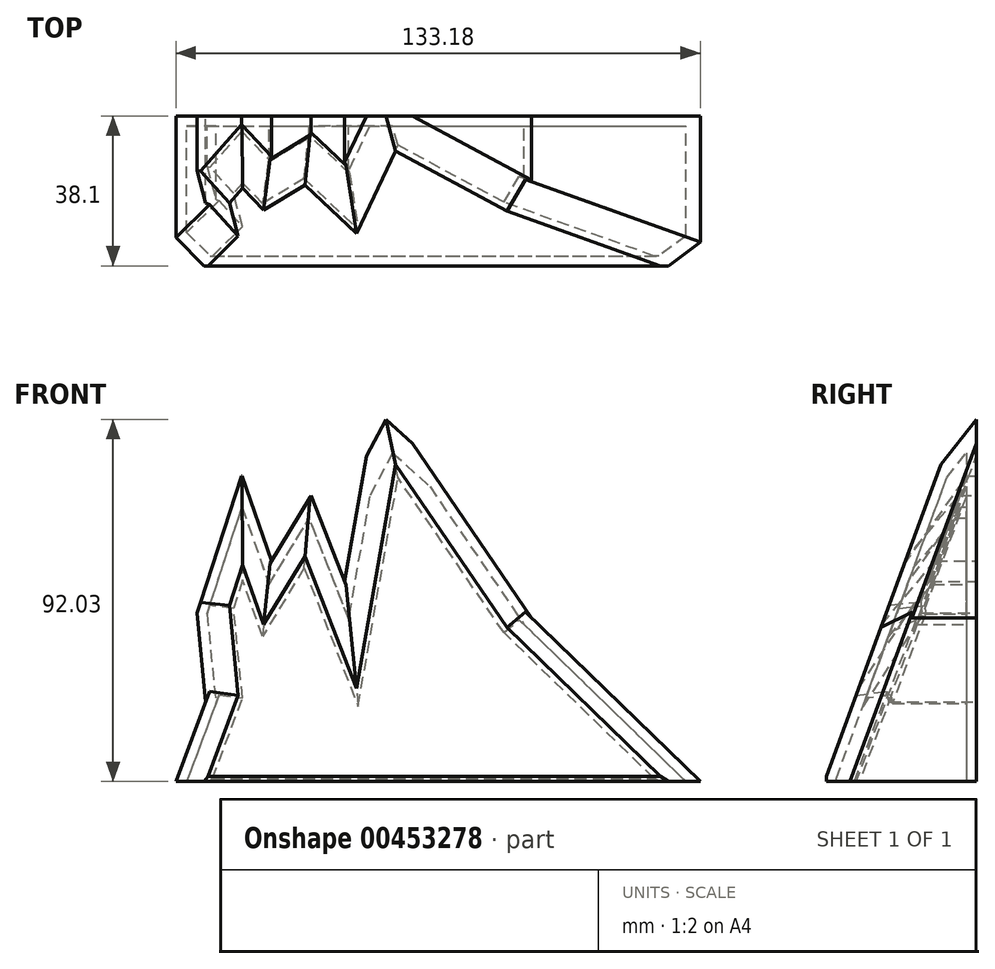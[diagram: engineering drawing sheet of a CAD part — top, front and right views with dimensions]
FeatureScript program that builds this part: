
annotation { "Feature Type Name" : "Feature", "Feature Type Description" : "" }
export const myFeature = defineFeature(function(context is Context, id is Id, definition is map)
    precondition{}
    {
        {
            var Q0;
            Q0=qCreatedBy(makeId("Front.planeOp"),FACE);
            var sketch = newSketch(context, id + "F0", { "sketchPlane" : qUnion([Q0])});
            skLineSegment(sketch, "E0", {"start": v(-64.04, -23.03) * mm, "end": v(69.14, -23.03) * mm});
            skLineSegment(sketch, "E1", {"start": v(-12.84, 75.84) * mm, "end": v(-21.19, 27.85) * mm});
            skLineSegment(sketch, "E2", {"start": v(-21.19, 27.85) * mm, "end": v(-29.7, 49.6) * mm});
            skLineSegment(sketch, "E3", {"start": v(-58.74, 19.82) * mm, "end": v(-56.5, -2.8) * mm});
            skLineSegment(sketch, "E4", {"start": v(-56.5, -2.8) * mm, "end": v(-64.04, -23.03) * mm});
            skLineSegment(sketch, "E5", {"start": v(-58.74, 19.82) * mm, "end": v(-47.35, 54.65) * mm});
            skLineSegment(sketch, "E6", {"start": v(-47.35, 54.65) * mm, "end": v(-39.8, 32.98) * mm});
            skLineSegment(sketch, "E7", {"start": v(-39.8, 32.98) * mm, "end": v(-29.7, 49.6) * mm});
            skLineSegment(sketch, "E8", {"start": v(-12.84, 75.84) * mm, "end": v(26.32, 18.54) * mm});
            skLineSegment(sketch, "E9", {"start": v(26.32, 18.54) * mm, "end": v(69.14, -23.03) * mm});
            skSolve(sketch);
        }
        {
            var Q0;
            Q0 = qSketchRegion(id + "F0", true);
            extrude(context, id + "F1", {"entities" : qUnion([Q0]), "depth" : 38.1 * mm});
        }
        {
            var Q0;
            Q0=qCreatedBy(makeId("Right.planeOp"),FACE);
            cPlane(context, id + "F2", {"entities" : qUnion([Q0]), "cplaneType" : CPlaneType.OFFSET, "offset" : 76.2 * mm, "width" : 152.4 * mm, "height" : 152.4 * mm});
        }
        {
            var Q0;
            Q0=qCreatedBy(id+"F2.planeOp",FACE);
            var sketch = newSketch(context, id + "F3", { "sketchPlane" : qUnion([Q0])});
            skLineSegment(sketch, "E10", {"start": v(-38.62, -23.16) * mm, "end": v(-1.41, 77.93) * mm});
            skLineSegment(sketch, "E11", {"start": v(-1.41, 77.93) * mm, "end": v(-41.3, 77.93) * mm});
            skLineSegment(sketch, "E12", {"start": v(-41.3, 77.93) * mm, "end": v(-38.62, -23.16) * mm});
            skSolve(sketch);
        }
        {
            var Q0;
            Q0 = qSketchRegion(id + "F3", true);
            extrude(context, id + "F4", {"entities" : qUnion([Q0]), "operationType" : NewBodyOperationType.REMOVE, "endBound" : BoundingType.THROUGH_ALL, "oppositeDirection" : true, "depth" : 25.4 * mm});
        }
        {
            var Q0;
            Q0=makeQuery(id+"F4.boolean.opBoolean","INTERSECT",EDGE,{"derivedFrom":[makeQuery(id+"F1.opExtrude","SWEPT_FACE",FACE,{"disambiguationData":[OSD([sQuery(id+"F0.wireOp",EDGE,"E5")])]}),makeQuery(id+"F4.opExtrude","SWEPT_FACE",FACE,{"disambiguationData":[OSD([sQuery(id+"F3.wireOp",EDGE,"E10")])]})]});
            var Q1;
            Q1=makeQuery(id+"F4.boolean.opBoolean","INTERSECT",EDGE,{"derivedFrom":[makeQuery(id+"F1.opExtrude","SWEPT_FACE",FACE,{"disambiguationData":[OSD([sQuery(id+"F0.wireOp",EDGE,"E6")])]}),makeQuery(id+"F4.opExtrude","SWEPT_FACE",FACE,{"disambiguationData":[OSD([sQuery(id+"F3.wireOp",EDGE,"E10")])]})]});
            var Q2;
            Q2=makeQuery(id+"F4.boolean.opBoolean","INTERSECT",EDGE,{"derivedFrom":[makeQuery(id+"F1.opExtrude","SWEPT_FACE",FACE,{"disambiguationData":[OSD([sQuery(id+"F0.wireOp",EDGE,"E7")])]}),makeQuery(id+"F4.opExtrude","SWEPT_FACE",FACE,{"disambiguationData":[OSD([sQuery(id+"F3.wireOp",EDGE,"E10")])]})]});
            var Q3;
            Q3=makeQuery(id+"F4.boolean.opBoolean","INTERSECT",EDGE,{"derivedFrom":[makeQuery(id+"F1.opExtrude","SWEPT_FACE",FACE,{"disambiguationData":[OSD([sQuery(id+"F0.wireOp",EDGE,"E2")])]}),makeQuery(id+"F4.opExtrude","SWEPT_FACE",FACE,{"disambiguationData":[OSD([sQuery(id+"F3.wireOp",EDGE,"E10")])]})]});
            var Q4;
            Q4=makeQuery(id+"F4.boolean.opBoolean","INTERSECT",EDGE,{"derivedFrom":[makeQuery(id+"F1.opExtrude","SWEPT_FACE",FACE,{"disambiguationData":[OSD([sQuery(id+"F0.wireOp",EDGE,"E1")])]}),makeQuery(id+"F4.opExtrude","SWEPT_FACE",FACE,{"disambiguationData":[OSD([sQuery(id+"F3.wireOp",EDGE,"E10")])]})]});
            var Q5;
            Q5=makeQuery(id+"F4.boolean.opBoolean","INTERSECT",EDGE,{"derivedFrom":[makeQuery(id+"F1.opExtrude","SWEPT_FACE",FACE,{"disambiguationData":[OSD([sQuery(id+"F0.wireOp",EDGE,"E8")])]}),makeQuery(id+"F4.opExtrude","SWEPT_FACE",FACE,{"disambiguationData":[OSD([sQuery(id+"F3.wireOp",EDGE,"E10")])]})]});
            var Q6;
            Q6=makeQuery(id+"F4.boolean.opBoolean","INTERSECT",EDGE,{"derivedFrom":[makeQuery(id+"F1.opExtrude","SWEPT_FACE",FACE,{"disambiguationData":[OSD([sQuery(id+"F0.wireOp",EDGE,"E9")])]}),makeQuery(id+"F4.opExtrude","SWEPT_FACE",FACE,{"disambiguationData":[OSD([sQuery(id+"F3.wireOp",EDGE,"E10")])]})]});
            var Q7;
            Q7=makeQuery(id+"F4.boolean.opBoolean","INTERSECT",EDGE,{"derivedFrom":[makeQuery(id+"F1.opExtrude","SWEPT_FACE",FACE,{"disambiguationData":[OSD([sQuery(id+"F0.wireOp",EDGE,"E4")])]}),makeQuery(id+"F4.opExtrude","SWEPT_FACE",FACE,{"disambiguationData":[OSD([sQuery(id+"F3.wireOp",EDGE,"E10")])]})]});
            var Q8;
            Q8=makeQuery(id+"F4.boolean.opBoolean","INTERSECT",EDGE,{"derivedFrom":[makeQuery(id+"F1.opExtrude","SWEPT_FACE",FACE,{"disambiguationData":[OSD([sQuery(id+"F0.wireOp",EDGE,"E3")])]}),makeQuery(id+"F4.opExtrude","SWEPT_FACE",FACE,{"disambiguationData":[OSD([sQuery(id+"F3.wireOp",EDGE,"E10")])]})]});
            chamfer(context, id + "F5", {"entities" : qUnion([Q0, Q1, Q2, Q3, Q4, Q5, Q6, Q7, Q8]), "width" : 8.13 * mm, "tangentPropagation" : true});
        }
        {
            var Q0;
            Q0=makeQuery(id+"F1.opExtrude","SWEPT_FACE",FACE,{"disambiguationData":[OSD([sQuery(id+"F0.wireOp",EDGE,"E0")])]});
            shell(context, id + "F6", {"entities" : qUnion([Q0]), "thickness" : 2.54 * mm});
        }
    });
